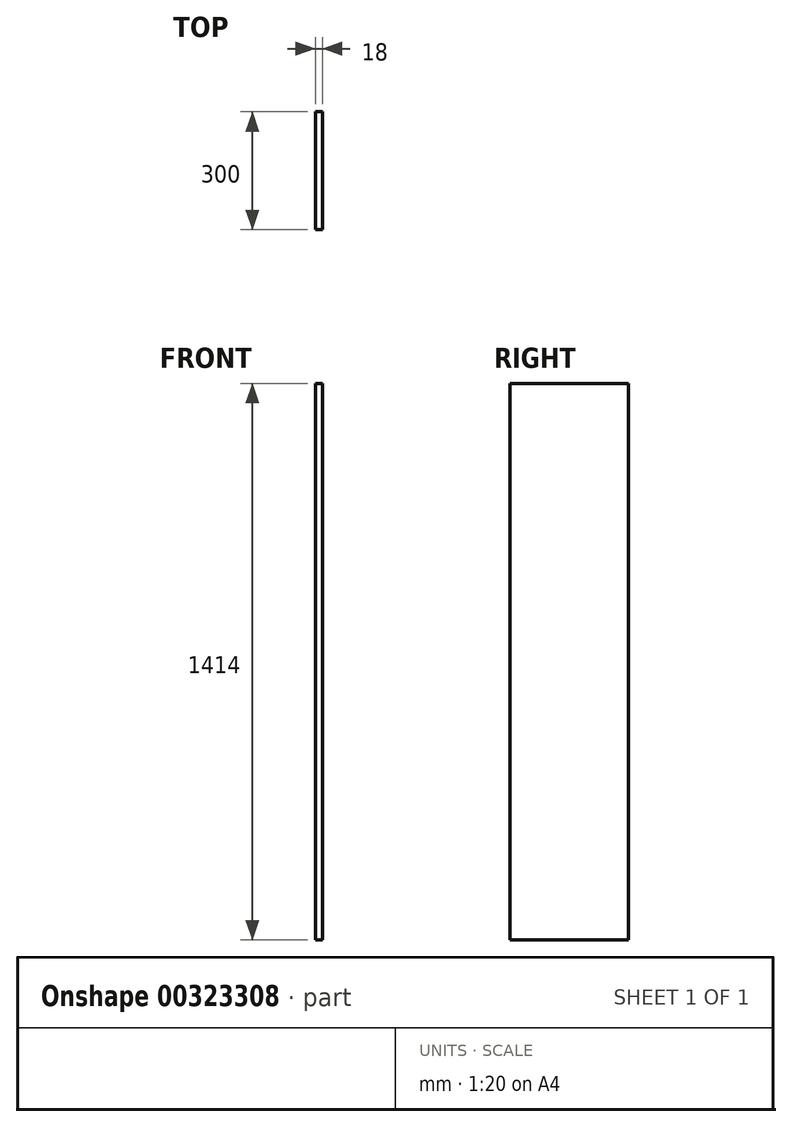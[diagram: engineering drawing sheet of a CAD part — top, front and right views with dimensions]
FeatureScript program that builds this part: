
annotation { "Feature Type Name" : "Feature", "Feature Type Description" : "" }
export const myFeature = defineFeature(function(context is Context, id is Id, definition is map)
    precondition{}
    {
        {
            var Q0;
            Q0=qCreatedBy(makeId("Right.planeOp"),FACE);
            var sketch = newSketch(context, id + "F0", { "sketchPlane" : qUnion([Q0])});
            skLineSegment(sketch, "E0.bottom", {"start": v(0, 0) * mm, "end": v(300, 0) * mm});
            skLineSegment(sketch, "E0.top", {"start": v(0, 1414) * mm, "end": v(300, 1414) * mm});
            skLineSegment(sketch, "E0.left", {"start": v(0, 0) * mm, "end": v(0, 1414) * mm});
            skLineSegment(sketch, "E0.right", {"start": v(300, 0) * mm, "end": v(300, 1414) * mm});
            skSolve(sketch);
        }
        {
            var Q0;
            Q0=qSketchRegion(id+"F0",true);
            extrude(context, id + "F1", {"entities" : qUnion([Q0]), "depth" : 18 * mm, "offsetDistance" : 25 * mm});
        }
    });
